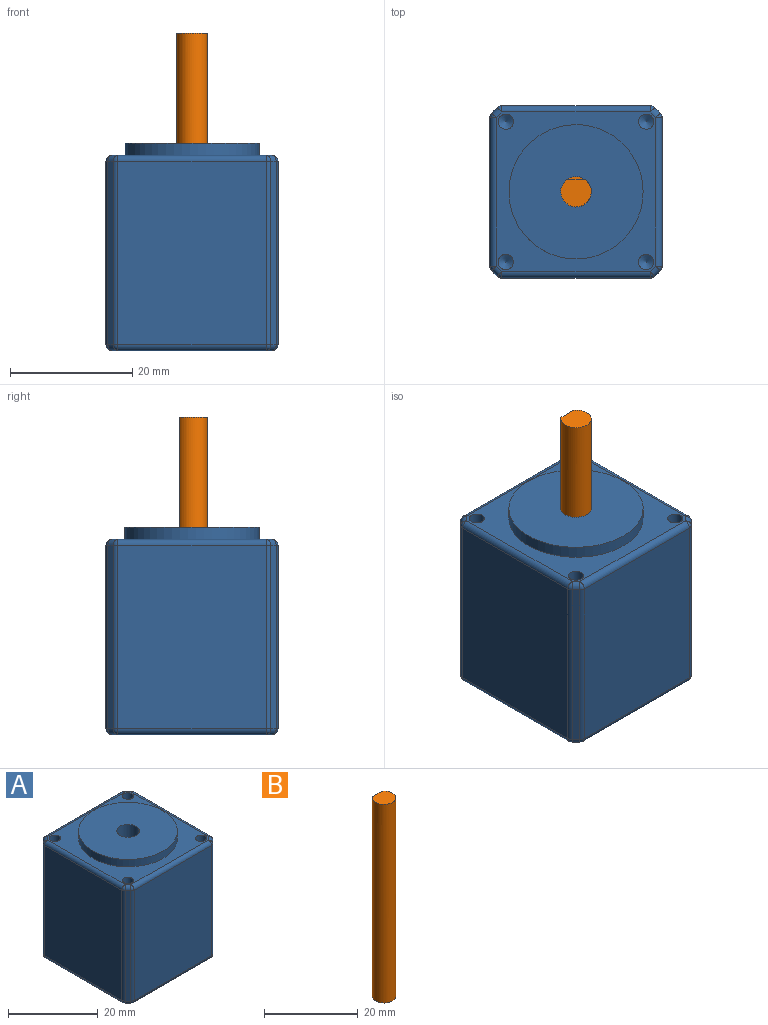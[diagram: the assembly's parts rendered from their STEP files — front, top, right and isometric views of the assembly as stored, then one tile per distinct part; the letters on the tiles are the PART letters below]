
ASSEMBLY  parts=2 mates=1
PART A: 61 faces, bbox 28.2x28.2x34 mm
  f0: plane 30x24.37mm, normal (1,0,0), area 731.1mm2, adj f39,f44,f48,f49
  f1: plane 30x24.37mm, normal (0,1,0), area 731.1mm2, adj f21,f24,f28,f29
  f2: plane 30x24.37mm, normal (-1,0,0), area 731.1mm2, adj f26,f35,f36,f37
  f3: plane 30x24.37mm, normal (0,-1,0), area 731.1mm2, adj f46,f55,f56,f60
  f4: plane 26.2x26.2mm, normal (0,0,-1), area 665.1mm2, adj f6,f24,f25,f34,f35,f44,f45,f54
  f5: plane 26.2x26.2mm, normal (0,0,1), area 285mm2, adj f7,f10,f12,f14,f16,f27,f28,f37
  f6: cylinder r=2.5mm len=34mm, axis (0,0,-1), area 534.1mm2, adj f4,f8
  f7: cylinder r=11mm len=22mm, axis (0,0,-1), area 138.2mm2, adj f5,f8
  f8: plane 22x22mm, normal (0,0,1), area 360.5mm2, adj f6,f7
  f9: cone r=0mm half-angle=59deg, axis (0,0,1), area 5.7mm2, adj f10
  f10: cylinder r=1.25mm len=6mm, axis (0,0,1), area 47.1mm2, adj f5,f9
  f11: cone r=0mm half-angle=59deg, axis (0,0,1), area 5.7mm2, adj f12
  f12: cylinder r=1.25mm len=6mm, axis (0,0,1), area 47.1mm2, adj f5,f11
  f13: cone r=0mm half-angle=59deg, axis (0,0,1), area 5.7mm2, adj f14
  f14: cylinder r=1.25mm len=6mm, axis (0,0,1), area 47.1mm2, adj f5,f13
  f15: cone r=0mm half-angle=59deg, axis (0,0,1), area 5.7mm2, adj f16
  f16: cylinder r=1.25mm len=6mm, axis (0,0,1), area 47.1mm2, adj f5,f15
  f17: plane 30x0.91mm, normal (-0.71,0.71,0), area 38.8mm2, adj f21,f25,f26,f27
  f18: plane 30x0.91mm, normal (0.71,0.71,0), area 38.8mm2, adj f29,f34,f38,f39
  f19: plane 30x0.91mm, normal (0.71,-0.71,0), area 38.8mm2, adj f49,f54,f57,f60
  f20: plane 30x0.91mm, normal (-0.71,-0.71,0), area 38.8mm2, adj f36,f45,f46,f47
  f21: cylinder r=1mm len=30mm, axis (0,0,-1), area 23.6mm2, adj f1,f17,f22,f23
  f22: sphere r=1mm, area 0.8mm2, adj f21,f24,f25
  f23: sphere r=1mm, area 0.8mm2, adj f21,f27,f28
  f24: cylinder r=1mm len=24.37mm, axis (1,0,0), area 38.3mm2, adj f1,f4,f22,f30
  f25: cylinder r=1mm len=1.62mm, axis (0.71,0.71,0), area 2mm2, adj f4,f17,f22,f31
  f26: cylinder r=1mm len=30mm, axis (0,0,1), area 23.6mm2, adj f2,f17,f31,f32
  f27: cylinder r=1mm len=1.62mm, axis (0.71,0.71,0), area 2mm2, adj f5,f17,f23,f32
  f28: cylinder r=1mm len=24.37mm, axis (-1,0,0), area 38.3mm2, adj f1,f5,f23,f33
  f29: cylinder r=1mm len=30mm, axis (0,0,-1), area 23.6mm2, adj f1,f18,f30,f33
  f30: sphere r=1mm, area 0.8mm2, adj f24,f29,f34
  f31: sphere r=1mm, area 0.8mm2, adj f25,f26,f35
  f32: sphere r=1mm, area 0.8mm2, adj f26,f27,f37
  f33: sphere r=1mm, area 0.8mm2, adj f28,f29,f38
  f34: cylinder r=1mm len=1.62mm, axis (-0.71,0.71,0), area 2mm2, adj f4,f18,f30,f40
  f35: cylinder r=1mm len=24.37mm, axis (0,1,0), area 38.3mm2, adj f2,f4,f31,f41
  f36: cylinder r=1mm len=30mm, axis (0,0,1), area 23.6mm2, adj f2,f20,f41,f42
  f37: cylinder r=1mm len=24.37mm, axis (0,-1,0), area 38.3mm2, adj f2,f5,f32,f42
  f38: cylinder r=1mm len=1.62mm, axis (-0.71,0.71,0), area 2mm2, adj f5,f18,f33,f43
  f39: cylinder r=1mm len=30mm, axis (0,0,-1), area 23.6mm2, adj f0,f18,f40,f43
  f40: sphere r=1mm, area 0.8mm2, adj f34,f39,f44
  f41: sphere r=1mm, area 0.8mm2, adj f35,f36,f45
  f42: sphere r=1mm, area 0.8mm2, adj f36,f37,f47
  f43: sphere r=1mm, area 0.8mm2, adj f38,f39,f48
  f44: cylinder r=1mm len=24.37mm, axis (0,-1,0), area 38.3mm2, adj f0,f4,f40,f50
  f45: cylinder r=1mm len=1.62mm, axis (0.71,-0.71,0), area 2mm2, adj f4,f20,f41,f51
  f46: cylinder r=1mm len=30mm, axis (0,0,1), area 23.6mm2, adj f3,f20,f51,f52
  f47: cylinder r=1mm len=1.62mm, axis (0.71,-0.71,0), area 2mm2, adj f5,f20,f42,f52
  f48: cylinder r=1mm len=24.37mm, axis (0,1,0), area 38.3mm2, adj f0,f5,f43,f53
  f49: cylinder r=1mm len=30mm, axis (0,0,-1), area 23.6mm2, adj f0,f19,f50,f53
  f50: sphere r=1mm, area 0.8mm2, adj f44,f49,f54
  f51: sphere r=1mm, area 0.8mm2, adj f45,f46,f55
  f52: sphere r=1mm, area 0.8mm2, adj f46,f47,f56
  f53: sphere r=1mm, area 0.8mm2, adj f48,f49,f57
  f54: cylinder r=1mm len=1.62mm, axis (-0.71,-0.71,0), area 2mm2, adj f4,f19,f50,f58
  f55: cylinder r=1mm len=24.37mm, axis (-1,0,0), area 38.3mm2, adj f3,f4,f51,f58
  f56: cylinder r=1mm len=24.37mm, axis (1,0,0), area 38.3mm2, adj f3,f5,f52,f59
  f57: cylinder r=1mm len=1.62mm, axis (-0.71,-0.71,0), area 2mm2, adj f5,f19,f53,f59
  f58: sphere r=1mm, area 0.8mm2, adj f54,f55,f60
  f59: sphere r=1mm, area 0.8mm2, adj f56,f57,f60
  f60: cylinder r=1mm len=30mm, axis (0,0,1), area 23.6mm2, adj f3,f19,f58,f59
PART B: 5 faces, bbox 5x5x52 mm
  f0: cylinder r=2.5mm len=52mm, axis (0,0,-1), area 752.5mm2, adj f1,f2,f3,f4
  f1: plane 5x4.5mm, normal (0,0,1), area 18.6mm2, adj f0,f3
  f2: plane 5x5mm, normal (0,0,-1), area 19.6mm2, adj f0
  f3: plane 20x3mm, normal (0,1,0), area 60mm2, adj f0,f1,f4
  f4: plane 3x0.5mm, normal (0,0,1), area 1mm2, adj f0,f3
PLACE A at identity
PLACE B t=(0,0,-6)mm
MATE revolute B.f0 <-> A.f6  axis (0,0,-1) through (0,0,-32)mm
